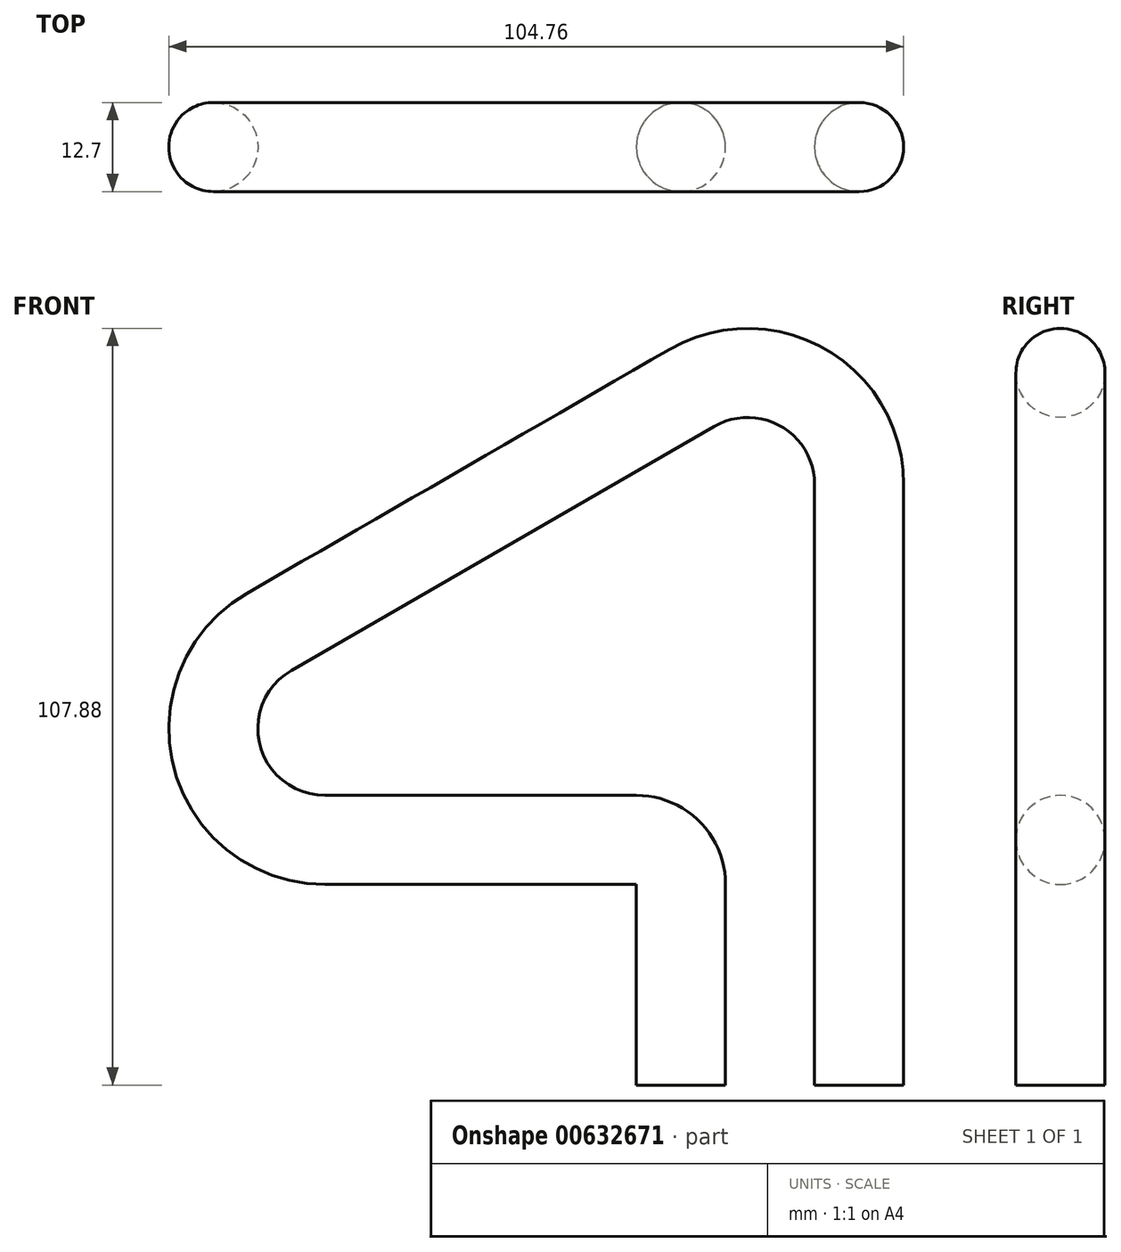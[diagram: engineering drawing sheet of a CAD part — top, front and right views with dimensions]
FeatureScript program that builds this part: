
annotation { "Feature Type Name" : "Feature", "Feature Type Description" : "" }
export const myFeature = defineFeature(function(context is Context, id is Id, definition is map)
    precondition{}
    {
        {
            var Q0;
            Q0=qCreatedBy(makeId("Front.planeOp"),FACE);
            var sketch = newSketch(context, id + "F0", { "sketchPlane" : qUnion([Q0])});
            skLineSegment(sketch, "E0", {"start": v(64.05, 63.9) * mm, "end": v(64.05, 149.54) * mm});
            skLineSegment(sketch, "E1", {"start": v(40.24, 163.3) * mm, "end": v(-20.07, 128.47) * mm});
            skLineSegment(sketch, "E2", {"start": v(-12.13, 98.85) * mm, "end": v(32.3, 98.85) * mm});
            skLineSegment(sketch, "E3", {"start": v(38.65, 92.5) * mm, "end": v(38.65, 63.9) * mm});
            skPoint(sketch, "E4.visualSharp", {"position": v(64.05, 177.04) * mm});
            skArc(sketch, "E4.filletArc", {"start": v(64.05, 149.54) * mm, "mid": v(56.11, 163.3) * mm, "end": v(40.24, 163.3) * mm});
            skPoint(sketch, "E5.visualSharp", {"position": v(38.65, 98.85) * mm});
            skArc(sketch, "E5.filletArc", {"start": v(38.65, 92.5) * mm, "mid": v(36.79, 97) * mm, "end": v(32.3, 98.85) * mm});
            skPoint(sketch, "E6.visualSharp", {"position": v(-71.38, 98.85) * mm});
            skArc(sketch, "E6.filletArc", {"start": v(-20.07, 128.47) * mm, "mid": v(-27.47, 110.62) * mm, "end": v(-12.13, 98.85) * mm});
            skLineSegment(sketch, "E7", {"start": v(16.34, 165.42) * mm, "end": v(60.22, 165.42) * mm, "construction": true});
            skSolve(sketch);
        }
        {
            var Q0;
            Q0=sQuery(id+"F0.wireOp",VERTEX,"E0.start");
            var Q1;
            Q1=sQuery(id+"F0.wireOp",EDGE,"E0");
            cPlane(context, id + "F1", {"entities" : qUnion([Q0, Q1]), "cplaneType" : CPlaneType.LINE_POINT, "offset" : 25.4 * mm, "width" : 152.4 * mm, "height" : 152.4 * mm});
        }
        {
            var Q0;
            Q0=qCreatedBy(id+"F1.planeOp",FACE);
            var sketch = newSketch(context, id + "F2", { "sketchPlane" : qUnion([Q0])});
            skCircle(sketch, "E8", {"center": v(64.05, 0) * mm, "radius": 6.35 * mm});
            skSolve(sketch);
        }
        {
            var Q0;
            Q0=makeQuery(id+"F2.imprint","IMPRINT",FACE,{"disambiguationData":[TD([[makeQuery(id+"F2.imprint","IMPRINT",EDGE,{"derivedFrom":sQuery(id+"F2.wireOp",EDGE,"E8")}),1.0]])]});
            var Q1;
            Q1 = qConstructionFilter(qBodyType(qCreatedBy(id + "F0" ,EDGE), BodyType.WIRE), ConstructionObject.NO);
            sweep(context, id + "F3", {"profiles" : qUnion([Q0]), "path" : qUnion([Q1])});
        }
    });
